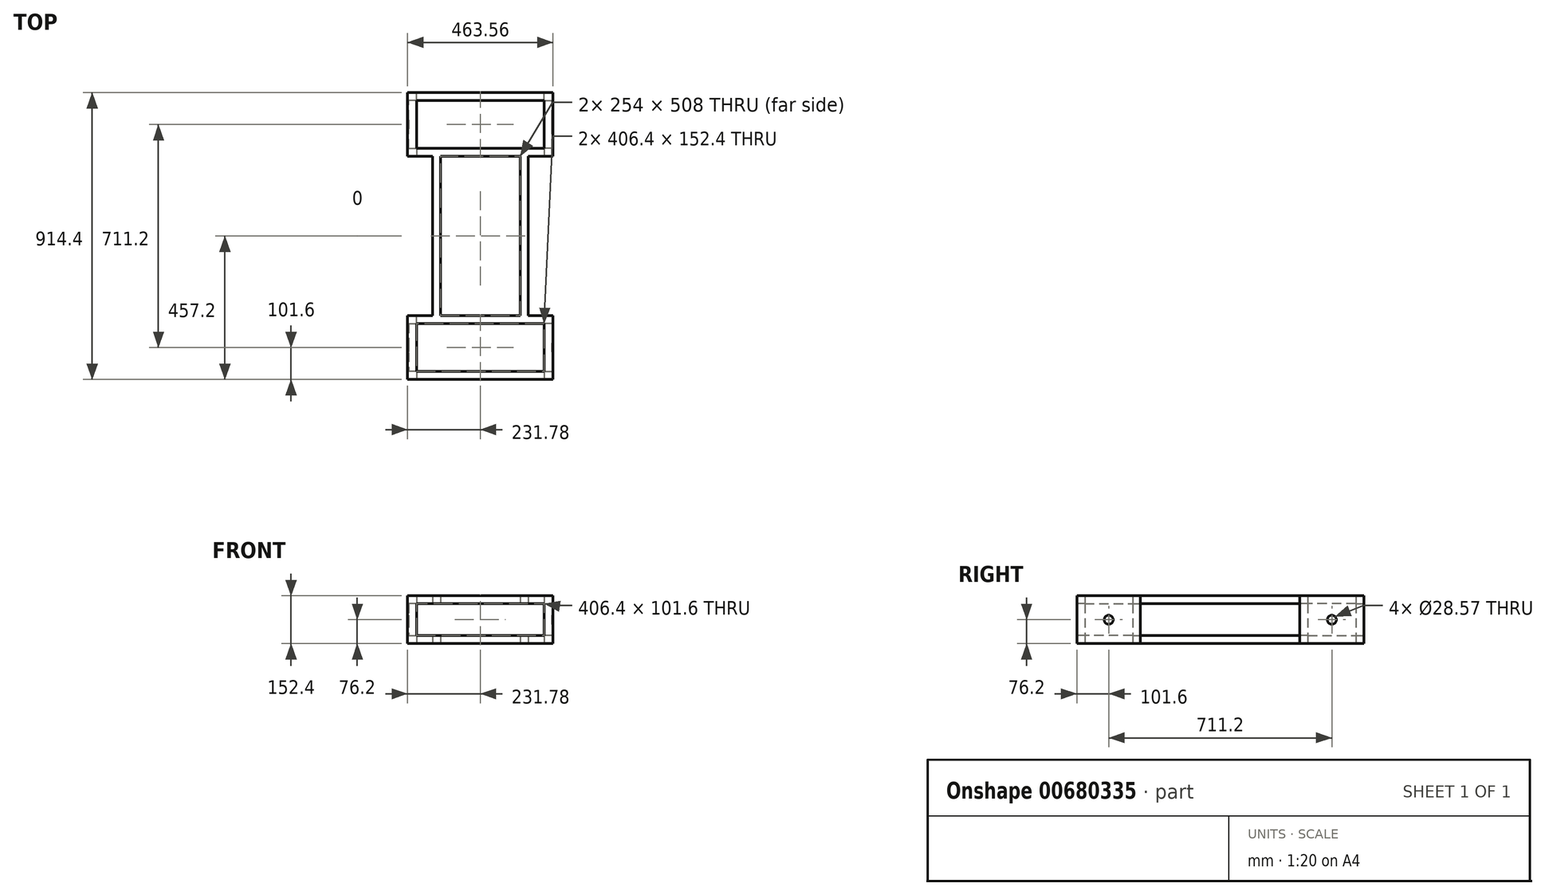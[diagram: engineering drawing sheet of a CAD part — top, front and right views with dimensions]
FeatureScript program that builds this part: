
annotation { "Feature Type Name" : "Feature", "Feature Type Description" : "" }
export const myFeature = defineFeature(function(context is Context, id is Id, definition is map)
    precondition{}
    {
        {
            var Q0;
            Q0=qCreatedBy(makeId("Top.planeOp"),FACE);
            var sketch = newSketch(context, id + "F0", { "sketchPlane" : qUnion([Q0])});
            skLineSegment(sketch, "E0.bottom", {"start": v(-228.6, 457.2) * mm, "end": v(228.6, 457.2) * mm});
            skLineSegment(sketch, "E0.top", {"start": v(-228.6, -457.2) * mm, "end": v(228.6, -457.2) * mm});
            skLineSegment(sketch, "E0.left", {"start": v(-228.6, 457.2) * mm, "end": v(-228.6, -457.2) * mm, "construction": true});
            skLineSegment(sketch, "E0.right", {"start": v(228.6, 457.2) * mm, "end": v(228.6, -457.2) * mm, "construction": true});
            skLineSegment(sketch, "E1.bottom", {"start": v(-203.2, 431.8) * mm, "end": v(203.2, 431.8) * mm});
            skLineSegment(sketch, "E1.top", {"start": v(-203.2, -431.8) * mm, "end": v(203.2, -431.8) * mm});
            skLineSegment(sketch, "E1.left", {"start": v(-203.2, 431.8) * mm, "end": v(-203.2, -431.8) * mm, "construction": true});
            skLineSegment(sketch, "E1.right", {"start": v(203.2, 431.8) * mm, "end": v(203.2, -431.8) * mm, "construction": true});
            skPoint(sketch, "E2", {"position": v(0, 431.8) * mm});
            skPoint(sketch, "E3", {"position": v(0, 457.2) * mm});
            skPoint(sketch, "E4", {"position": v(228.6, 0) * mm});
            skPoint(sketch, "E5", {"position": v(203.2, 0) * mm});
            skLineSegment(sketch, "E6.bottom", {"start": v(-203.2, -279.4) * mm, "end": v(203.2, -279.4) * mm});
            skLineSegment(sketch, "E6.top", {"start": v(-203.2, -254) * mm, "end": v(203.2, -254) * mm});
            skLineSegment(sketch, "E6.left", {"start": v(-203.2, -279.4) * mm, "end": v(-203.2, -254) * mm});
            skLineSegment(sketch, "E6.right", {"start": v(203.2, -279.4) * mm, "end": v(203.2, -254) * mm});
            skLineSegment(sketch, "E7.MirrorCS", {"start": v(-203.2, 254) * mm, "end": v(203.2, 254) * mm});
            skLineSegment(sketch, "E8.MirrorCS", {"start": v(-203.2, 279.4) * mm, "end": v(203.2, 279.4) * mm});
            skLineSegment(sketch, "E9", {"start": v(0, 457.2) * mm, "end": v(0, -457.2) * mm, "construction": true});
            skLineSegment(sketch, "E10.bottom", {"start": v(-152.4, -254) * mm, "end": v(-127, -254) * mm});
            skLineSegment(sketch, "E10.top", {"start": v(-152.4, 254) * mm, "end": v(-127, 254) * mm});
            skLineSegment(sketch, "E10.left", {"start": v(-152.4, -254) * mm, "end": v(-152.4, 254) * mm});
            skLineSegment(sketch, "E10.right", {"start": v(-127, -254) * mm, "end": v(-127, 254) * mm});
            skLineSegment(sketch, "E11.MirrorCS", {"start": v(127, -254) * mm, "end": v(127, 254) * mm});
            skLineSegment(sketch, "E12.MirrorCS", {"start": v(152.4, -254) * mm, "end": v(152.4, 254) * mm});
            skLineSegment(sketch, "E13", {"start": v(-203.2, 254) * mm, "end": v(-228.6, 254) * mm});
            skLineSegment(sketch, "E14", {"start": v(-228.6, 254) * mm, "end": v(-228.6, 457.2) * mm});
            skLineSegment(sketch, "E15", {"start": v(-203.2, 431.8) * mm, "end": v(-203.2, 279.4) * mm});
            skLineSegment(sketch, "E16", {"start": v(-203.2, -254) * mm, "end": v(-228.6, -254) * mm});
            skLineSegment(sketch, "E17", {"start": v(-228.6, -254) * mm, "end": v(-228.6, -457.2) * mm});
            skLineSegment(sketch, "E18", {"start": v(-203.2, -431.8) * mm, "end": v(-203.2, -279.4) * mm});
            skLineSegment(sketch, "E19", {"start": v(203.2, -431.8) * mm, "end": v(203.2, -279.4) * mm});
            skLineSegment(sketch, "E20", {"start": v(203.2, -254) * mm, "end": v(228.6, -254) * mm});
            skLineSegment(sketch, "E21", {"start": v(228.6, -254) * mm, "end": v(228.6, -457.2) * mm});
            skLineSegment(sketch, "E22", {"start": v(203.2, 254) * mm, "end": v(228.6, 254) * mm});
            skLineSegment(sketch, "E23", {"start": v(228.6, 254) * mm, "end": v(228.6, 457.2) * mm});
            skLineSegment(sketch, "E24", {"start": v(203.2, 279.4) * mm, "end": v(203.2, 431.8) * mm});
            skSolve(sketch);
        }
        {
            var Q0;
            Q0 = qSketchRegion(id + "F0", true);
            var Q1;
            Q1=makeQuery(id+"F0.imprint","IMPRINT",FACE,{"disambiguationData":[TD([[makeQuery(id+"F0.imprint","IMPRINT",EDGE,{"derivedFrom":sQuery(id+"F0.wireOp",EDGE,"E6.bottom")}),1.0]])]});
            var Q2;
            {var subQ0=sQuery(id+"F0.wireOp",EDGE,"E7.MirrorCS");Q2=makeQuery(id+"F0.imprint","IMPRINT",FACE,{"disambiguationData":[TD([[makeQuery(id+"F0.imprint","IMPRINT",EDGE,{"derivedFrom":subQ0}),1.0]])]});}
            extrude(context, id + "F1", {"entities" : qUnion([Q0, Q1, Q2]), "depth" : 25.4 * mm, "offsetDistance" : 25.4 * mm});
        }
        {
            var Q0;
            Q0=makeQuery(id+"F1.opExtrude","CAP_FACE",FACE,{"disambiguationData":[OSD([sQuery(id+"F0.wireOp",EDGE,"E0.bottom"),sQuery(id+"F0.wireOp",EDGE,"E0.top"),sQuery(id+"F0.wireOp",EDGE,"E0.left"),sQuery(id+"F0.wireOp",EDGE,"E0.right"),sQuery(id+"F0.wireOp",EDGE,"E1.bottom"),sQuery(id+"F0.wireOp",EDGE,"E1.top"),sQuery(id+"F0.wireOp",EDGE,"E1.left"),sQuery(id+"F0.wireOp",EDGE,"E1.right")])],"isStart":false});
            var sketch = newSketch(context, id + "F2", { "sketchPlane" : qUnion([Q0])});
            skLineSegment(sketch, "E25.bottom", {"start": v(-203.2, -431.8) * mm, "end": v(-228.6, -431.8) * mm});
            skLineSegment(sketch, "E25.top", {"start": v(-203.2, -457.2) * mm, "end": v(-228.6, -457.2) * mm});
            skLineSegment(sketch, "E25.left", {"start": v(-203.2, -431.8) * mm, "end": v(-203.2, -457.2) * mm});
            skLineSegment(sketch, "E25.right", {"start": v(-228.6, -431.8) * mm, "end": v(-228.6, -457.2) * mm});
            skLineSegment(sketch, "E26.MirrorCS", {"start": v(-228.6, 431.8) * mm, "end": v(-228.6, 457.2) * mm});
            skLineSegment(sketch, "E27.MirrorCS", {"start": v(-203.2, 431.8) * mm, "end": v(-203.2, 457.2) * mm});
            skLineSegment(sketch, "E28.MirrorCS", {"start": v(-203.2, 457.2) * mm, "end": v(-228.6, 457.2) * mm});
            skLineSegment(sketch, "E29.MirrorCS", {"start": v(-203.2, 431.8) * mm, "end": v(-228.6, 431.8) * mm});
            skLineSegment(sketch, "E30.MirrorCS", {"start": v(203.2, 457.2) * mm, "end": v(228.6, 457.2) * mm});
            skLineSegment(sketch, "E31.MirrorCS", {"start": v(203.2, 431.8) * mm, "end": v(203.2, 457.2) * mm});
            skLineSegment(sketch, "E32.MirrorCS", {"start": v(228.6, 431.8) * mm, "end": v(228.6, 457.2) * mm});
            skLineSegment(sketch, "E33.MirrorCS", {"start": v(228.6, -431.8) * mm, "end": v(228.6, -457.2) * mm});
            skLineSegment(sketch, "E34.MirrorCS", {"start": v(203.2, -431.8) * mm, "end": v(203.2, -457.2) * mm});
            skLineSegment(sketch, "E35.MirrorCS", {"start": v(203.2, -457.2) * mm, "end": v(228.6, -457.2) * mm});
            skLineSegment(sketch, "E36.MirrorCS", {"start": v(203.2, -431.8) * mm, "end": v(228.6, -431.8) * mm});
            skLineSegment(sketch, "E37.MirrorCS", {"start": v(203.2, 431.8) * mm, "end": v(228.6, 431.8) * mm});
            skLineSegment(sketch, "E38.bottom", {"start": v(-228.6, -279.4) * mm, "end": v(-203.2, -279.4) * mm});
            skLineSegment(sketch, "E38.top", {"start": v(-228.6, -254) * mm, "end": v(-203.2, -254) * mm});
            skLineSegment(sketch, "E38.left", {"start": v(-228.6, -279.4) * mm, "end": v(-228.6, -254) * mm});
            skLineSegment(sketch, "E38.right", {"start": v(-203.2, -279.4) * mm, "end": v(-203.2, -254) * mm});
            skLineSegment(sketch, "E39.MirrorCS", {"start": v(-228.6, 279.4) * mm, "end": v(-228.6, 254) * mm});
            skLineSegment(sketch, "E40.MirrorCS", {"start": v(-228.6, 279.4) * mm, "end": v(-203.2, 279.4) * mm});
            skLineSegment(sketch, "E41.MirrorCS", {"start": v(-203.2, 279.4) * mm, "end": v(-203.2, 254) * mm});
            skLineSegment(sketch, "E42.MirrorCS", {"start": v(-228.6, 254) * mm, "end": v(-203.2, 254) * mm});
            skLineSegment(sketch, "E43.MirrorCS", {"start": v(228.6, -254) * mm, "end": v(203.2, -254) * mm});
            skLineSegment(sketch, "E44.MirrorCS", {"start": v(203.2, -279.4) * mm, "end": v(203.2, -254) * mm});
            skLineSegment(sketch, "E45.MirrorCS", {"start": v(228.6, 279.4) * mm, "end": v(203.2, 279.4) * mm});
            skLineSegment(sketch, "E46.MirrorCS", {"start": v(228.6, 254) * mm, "end": v(203.2, 254) * mm});
            skLineSegment(sketch, "E47.MirrorCS", {"start": v(203.2, 279.4) * mm, "end": v(203.2, 254) * mm});
            skLineSegment(sketch, "E48.MirrorCS", {"start": v(228.6, 279.4) * mm, "end": v(228.6, 254) * mm});
            skLineSegment(sketch, "E49.MirrorCS", {"start": v(228.6, -279.4) * mm, "end": v(203.2, -279.4) * mm});
            skLineSegment(sketch, "E50.MirrorCS", {"start": v(228.6, -279.4) * mm, "end": v(228.6, -254) * mm});
            skSolve(sketch);
        }
        {
            var Q0;
            Q0 = qSketchRegion(id + "F2", true);
            extrude(context, id + "F3", {"entities" : qUnion([Q0]), "operationType" : NewBodyOperationType.ADD, "depth" : 101.6 * mm, "offsetDistance" : 25.4 * mm});
        }
        {
            var Q0;
            Q0=makeQuery(id+"F3.opExtrude","CAP_FACE",FACE,{"disambiguationData":[OSD([sQuery(id+"F2.wireOp",EDGE,"E33.MirrorCS"),sQuery(id+"F2.wireOp",EDGE,"E34.MirrorCS"),sQuery(id+"F2.wireOp",EDGE,"E35.MirrorCS"),sQuery(id+"F2.wireOp",EDGE,"E36.MirrorCS")])],"isStart":false});
            var sketch = newSketch(context, id + "F4", { "sketchPlane" : qUnion([Q0])});
            skLineSegment(sketch, "E51.bottom", {"start": v(228.6, 457.2) * mm, "end": v(-228.6, 457.2) * mm});
            skLineSegment(sketch, "E51.top", {"start": v(228.6, 431.8) * mm, "end": v(-228.6, 431.8) * mm});
            skLineSegment(sketch, "E51.left", {"start": v(228.6, 457.2) * mm, "end": v(228.6, 431.8) * mm});
            skLineSegment(sketch, "E51.right", {"start": v(-228.6, 457.2) * mm, "end": v(-228.6, 431.8) * mm});
            skLineSegment(sketch, "E52.bottom", {"start": v(228.6, 431.8) * mm, "end": v(203.2, 431.8) * mm});
            skLineSegment(sketch, "E52.top", {"start": v(228.6, 254) * mm, "end": v(203.2, 254) * mm});
            skLineSegment(sketch, "E52.left", {"start": v(228.6, 431.8) * mm, "end": v(228.6, 254) * mm});
            skLineSegment(sketch, "E52.right", {"start": v(203.2, 431.8) * mm, "end": v(203.2, 254) * mm});
            skLineSegment(sketch, "E53.MirrorCS", {"start": v(-203.2, 431.8) * mm, "end": v(-203.2, 254) * mm});
            skLineSegment(sketch, "E54.MirrorCS", {"start": v(-228.6, 431.8) * mm, "end": v(-228.6, 254) * mm});
            skLineSegment(sketch, "E55.MirrorCS", {"start": v(-228.6, 254) * mm, "end": v(-203.2, 254) * mm});
            skLineSegment(sketch, "E56.bottom", {"start": v(203.2, 254) * mm, "end": v(-203.2, 254) * mm});
            skLineSegment(sketch, "E56.top", {"start": v(203.2, 279.4) * mm, "end": v(-203.2, 279.4) * mm});
            skLineSegment(sketch, "E56.left", {"start": v(203.2, 254) * mm, "end": v(203.2, 279.4) * mm});
            skLineSegment(sketch, "E56.right", {"start": v(-203.2, 254) * mm, "end": v(-203.2, 279.4) * mm});
            skLineSegment(sketch, "E57.bottom", {"start": v(152.4, 254) * mm, "end": v(127, 254) * mm});
            skLineSegment(sketch, "E57.top", {"start": v(152.4, -254) * mm, "end": v(127, -254) * mm});
            skLineSegment(sketch, "E57.left", {"start": v(152.4, 254) * mm, "end": v(152.4, -254) * mm});
            skLineSegment(sketch, "E57.right", {"start": v(127, 254) * mm, "end": v(127, -254) * mm});
            skLineSegment(sketch, "E58.MirrorCS", {"start": v(-152.4, 254) * mm, "end": v(-152.4, -254) * mm});
            skLineSegment(sketch, "E59.MirrorCS", {"start": v(-127, 254) * mm, "end": v(-127, -254) * mm});
            skLineSegment(sketch, "E60.MirrorCS", {"start": v(228.6, -431.8) * mm, "end": v(203.2, -431.8) * mm});
            skLineSegment(sketch, "E61.MirrorCS", {"start": v(-228.6, -457.2) * mm, "end": v(-228.6, -431.8) * mm});
            skLineSegment(sketch, "E62.MirrorCS", {"start": v(228.6, -457.2) * mm, "end": v(228.6, -431.8) * mm});
            skLineSegment(sketch, "E63.MirrorCS", {"start": v(228.6, -254) * mm, "end": v(203.2, -254) * mm});
            skLineSegment(sketch, "E64.MirrorCS", {"start": v(-228.6, -254) * mm, "end": v(-203.2, -254) * mm});
            skLineSegment(sketch, "E65.MirrorCS", {"start": v(203.2, -254) * mm, "end": v(203.2, -279.4) * mm});
            skLineSegment(sketch, "E66.MirrorCS", {"start": v(-203.2, -254) * mm, "end": v(-203.2, -279.4) * mm});
            skLineSegment(sketch, "E67.MirrorCS", {"start": v(228.6, -457.2) * mm, "end": v(-228.6, -457.2) * mm});
            skLineSegment(sketch, "E68.MirrorCS", {"start": v(203.2, -431.8) * mm, "end": v(203.2, -254) * mm});
            skLineSegment(sketch, "E69.MirrorCS", {"start": v(203.2, -254) * mm, "end": v(-203.2, -254) * mm});
            skLineSegment(sketch, "E70.MirrorCS", {"start": v(203.2, -279.4) * mm, "end": v(-203.2, -279.4) * mm});
            skLineSegment(sketch, "E71.MirrorCS", {"start": v(-228.6, -431.8) * mm, "end": v(-228.6, -254) * mm});
            skLineSegment(sketch, "E72.MirrorCS", {"start": v(-203.2, -431.8) * mm, "end": v(-203.2, -254) * mm});
            skLineSegment(sketch, "E73.MirrorCS", {"start": v(228.6, -431.8) * mm, "end": v(-228.6, -431.8) * mm});
            skLineSegment(sketch, "E74.MirrorCS", {"start": v(228.6, -431.8) * mm, "end": v(228.6, -254) * mm});
            skSolve(sketch);
        }
        {
            var Q0;
            Q0 = qSketchRegion(id + "F4", true);
            extrude(context, id + "F5", {"entities" : qUnion([Q0]), "operationType" : NewBodyOperationType.ADD, "depth" : 25.4 * mm, "offsetDistance" : 25.4 * mm});
        }
        {
            var Q0;
            Q0=makeQuery(id+"F5.boolean.opBoolean","MERGE",FACE,{"derivedFrom":[makeQuery(id+"F3.boolean.opBoolean","MERGE",FACE,{"derivedFrom":[makeQuery(id+"F1.opExtrude","SWEPT_FACE",FACE,{"disambiguationData":[OSD([sQuery(id+"F0.wireOp",EDGE,"E0.right")])]}),makeQuery(id+"F3.opExtrude","SWEPT_FACE",FACE,{"disambiguationData":[OSD([sQuery(id+"F2.wireOp",EDGE,"E32.MirrorCS")])]}),makeQuery(id+"F3.opExtrude","SWEPT_FACE",FACE,{"disambiguationData":[OSD([sQuery(id+"F2.wireOp",EDGE,"E33.MirrorCS")])]}),makeQuery(id+"F3.opExtrude","SWEPT_FACE",FACE,{"disambiguationData":[OSD([sQuery(id+"F2.wireOp",EDGE,"E48.MirrorCS")])]}),makeQuery(id+"F3.opExtrude","SWEPT_FACE",FACE,{"disambiguationData":[OSD([sQuery(id+"F2.wireOp",EDGE,"E50.MirrorCS")])]})]}),makeQuery(id+"F5.opExtrude","SWEPT_FACE",FACE,{"disambiguationData":[OSD([sQuery(id+"F4.wireOp",EDGE,"Wdg1V6kY-x6Q8-cJW5-QTke-MaLvcnpzVtc4.right")])]})]});
            var sketch = newSketch(context, id + "F6", { "sketchPlane" : qUnion([Q0])});
            skLineSegment(sketch, "E75.bottom", {"start": v(-457.2, 152.4) * mm, "end": v(-254, 152.4) * mm});
            skLineSegment(sketch, "E75.top", {"start": v(-457.2, 0) * mm, "end": v(-254, 0) * mm});
            skLineSegment(sketch, "E75.left", {"start": v(-457.2, 152.4) * mm, "end": v(-457.2, 0) * mm});
            skLineSegment(sketch, "E75.right", {"start": v(-254, 152.4) * mm, "end": v(-254, 0) * mm});
            skLineSegment(sketch, "E76.MirrorCS", {"start": v(457.2, 152.4) * mm, "end": v(254, 152.4) * mm});
            skLineSegment(sketch, "E77.MirrorCS", {"start": v(457.2, 0) * mm, "end": v(254, 0) * mm});
            skLineSegment(sketch, "E78.MirrorCS", {"start": v(457.2, 152.4) * mm, "end": v(457.2, 0) * mm});
            skLineSegment(sketch, "E79.MirrorCS", {"start": v(254, 152.4) * mm, "end": v(254, 0) * mm});
            skSolve(sketch);
        }
        {
            var Q0;
            Q0 = qSketchRegion(id + "F6", true);
            extrude(context, id + "F7", {"entities" : qUnion([Q0]), "operationType" : NewBodyOperationType.ADD, "depth" : 3.17 * mm, "offsetDistance" : 25.4 * mm});
        }
        {
            var Q0;
            Q0=makeQuery(id+"F5.boolean.opBoolean","MERGE",FACE,{"derivedFrom":[makeQuery(id+"F3.boolean.opBoolean","MERGE",FACE,{"derivedFrom":[makeQuery(id+"F1.opExtrude","SWEPT_FACE",FACE,{"disambiguationData":[OSD([sQuery(id+"F0.wireOp",EDGE,"E0.left")])]}),makeQuery(id+"F3.opExtrude","SWEPT_FACE",FACE,{"disambiguationData":[OSD([sQuery(id+"F2.wireOp",EDGE,"E25.right")])]}),makeQuery(id+"F3.opExtrude","SWEPT_FACE",FACE,{"disambiguationData":[OSD([sQuery(id+"F2.wireOp",EDGE,"E26.MirrorCS")])]}),makeQuery(id+"F3.opExtrude","SWEPT_FACE",FACE,{"disambiguationData":[OSD([sQuery(id+"F2.wireOp",EDGE,"E38.left")])]}),makeQuery(id+"F3.opExtrude","SWEPT_FACE",FACE,{"disambiguationData":[OSD([sQuery(id+"F2.wireOp",EDGE,"E39.MirrorCS")])]})]}),makeQuery(id+"F5.opExtrude","SWEPT_FACE",FACE,{"disambiguationData":[OSD([sQuery(id+"F4.wireOp",EDGE,"Wdg1V6kY-x6Q8-cJW5-QTke-MaLvcnpzVtc4.left")])]})]});
            var sketch = newSketch(context, id + "F8", { "sketchPlane" : qUnion([Q0])});
            skLineSegment(sketch, "E80.bottom", {"start": v(-457.2, 152.4) * mm, "end": v(-254, 152.4) * mm});
            skLineSegment(sketch, "E80.top", {"start": v(-457.2, 0) * mm, "end": v(-254, 0) * mm});
            skLineSegment(sketch, "E80.left", {"start": v(-457.2, 152.4) * mm, "end": v(-457.2, 0) * mm});
            skLineSegment(sketch, "E80.right", {"start": v(-254, 152.4) * mm, "end": v(-254, 0) * mm});
            skLineSegment(sketch, "E81.MirrorCS", {"start": v(457.2, 152.4) * mm, "end": v(254, 152.4) * mm});
            skLineSegment(sketch, "E82.MirrorCS", {"start": v(457.2, 0) * mm, "end": v(254, 0) * mm});
            skLineSegment(sketch, "E83.MirrorCS", {"start": v(254, 152.4) * mm, "end": v(254, 0) * mm});
            skLineSegment(sketch, "E84.MirrorCS", {"start": v(457.2, 152.4) * mm, "end": v(457.2, 0) * mm});
            skSolve(sketch);
        }
        {
            var Q0;
            Q0 = qSketchRegion(id + "F8", true);
            extrude(context, id + "F9", {"entities" : qUnion([Q0]), "operationType" : NewBodyOperationType.ADD, "depth" : 3.17 * mm, "offsetDistance" : 25.4 * mm});
        }
        {
            var Q0;
            Q0=makeQuery(id+"F7.opExtrude","CAP_FACE",FACE,{"disambiguationData":[OSD([sQuery(id+"F6.wireOp",EDGE,"E76.MirrorCS"),sQuery(id+"F6.wireOp",EDGE,"E77.MirrorCS"),sQuery(id+"F6.wireOp",EDGE,"E78.MirrorCS"),sQuery(id+"F6.wireOp",EDGE,"E79.MirrorCS")])],"isStart":false});
            var sketch = newSketch(context, id + "F10", { "sketchPlane" : qUnion([Q0])});
            skLineSegment(sketch, "E85", {"start": v(457.2, 76.2) * mm, "end": v(254, 76.2) * mm, "construction": true});
            skCircle(sketch, "E86", {"center": v(355.6, 76.2) * mm, "radius": 14.29 * mm});
            skPoint(sketch, "E87.MirrorP", {"position": v(-355.6, 76.2) * mm});
            skCircle(sketch, "E88.MirrorC", {"center": v(-355.6, 76.2) * mm, "radius": 14.29 * mm});
            skLineSegment(sketch, "E89.MirrorCS", {"start": v(-457.2, 76.2) * mm, "end": v(-254, 76.2) * mm, "construction": true});
            skSolve(sketch);
        }
        {
            var Q0;
            Q0 = qSketchRegion(id + "F10", true);
            extrude(context, id + "F11", {"entities" : qUnion([Q0]), "operationType" : NewBodyOperationType.REMOVE, "endBound" : BoundingType.THROUGH_ALL, "oppositeDirection" : true, "depth" : 25.4 * mm, "offsetDistance" : 25.4 * mm});
        }
    });
